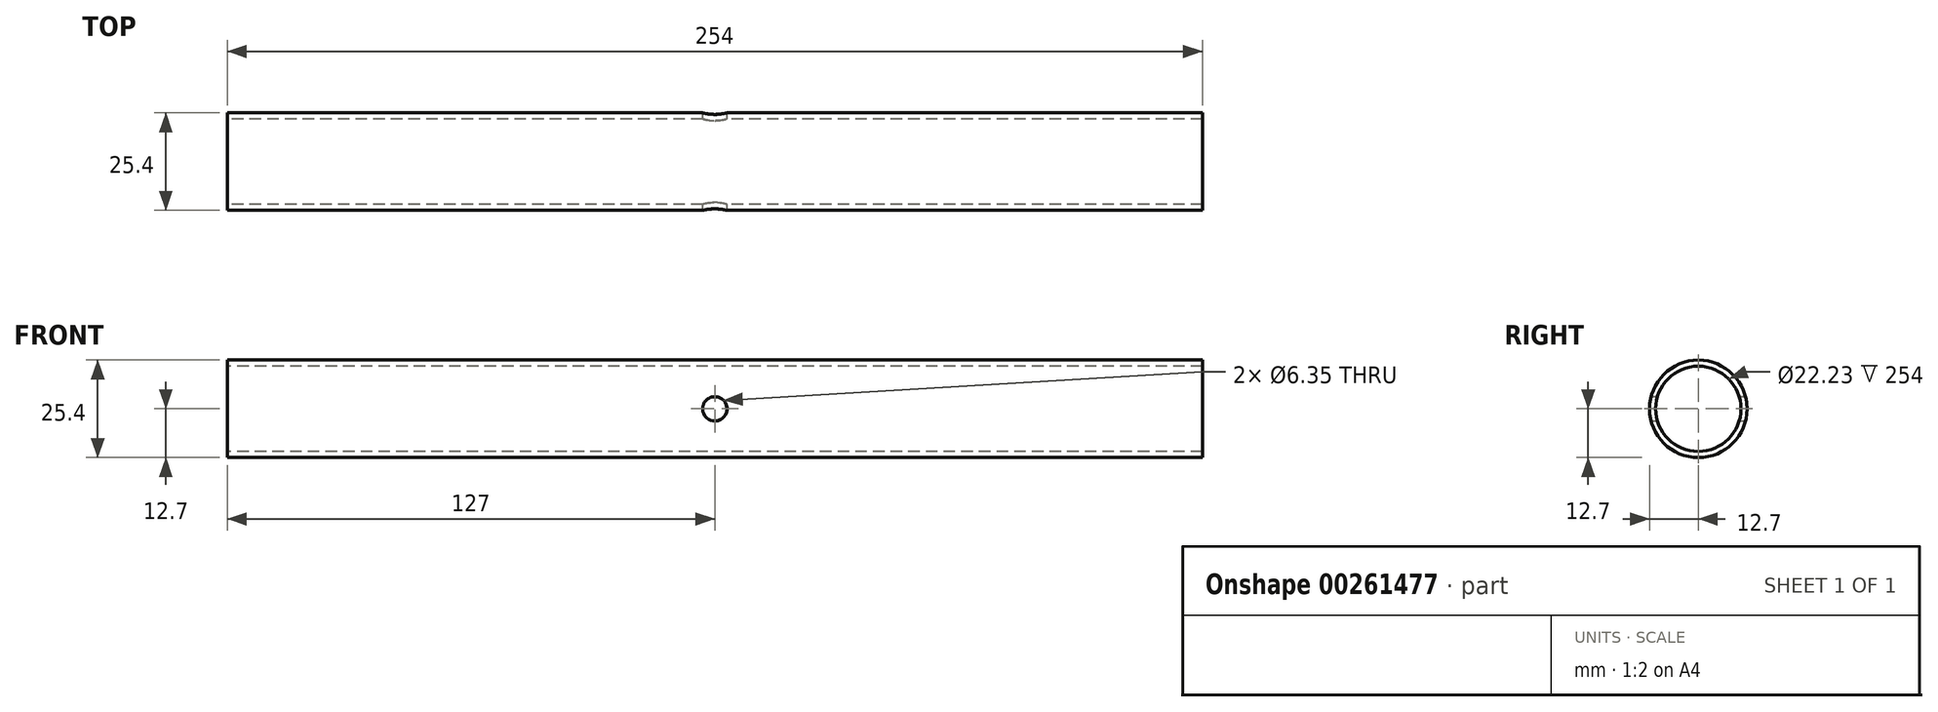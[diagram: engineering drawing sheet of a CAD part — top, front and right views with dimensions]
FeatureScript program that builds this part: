
annotation { "Feature Type Name" : "Feature", "Feature Type Description" : "" }
export const myFeature = defineFeature(function(context is Context, id is Id, definition is map)
    precondition{}
    {
        {
            var Q0;
            Q0=qCreatedBy(makeId("Right.planeOp"),FACE);
            var sketch = newSketch(context, id + "F0", { "sketchPlane" : qUnion([Q0])});
            skCircle(sketch, "E0", {"center": v(-12.7, 0) * mm, "radius": 12.7 * mm});
            skCircle(sketch, "E1", {"center": v(-12.7, 0) * mm, "radius": 11.11 * mm});
            skSolve(sketch);
        }
        {
            var Q0;
            Q0=makeQuery(id+"F0.imprint","IMPRINT",FACE,{"disambiguationData":[TD([[makeQuery(id+"F0.imprint","IMPRINT",EDGE,{"derivedFrom":sQuery(id+"F0.wireOp",EDGE,"E0")}),1.0]])]});
            extrude(context, id + "F3", {"entities" : qUnion([Q0]), "depth" : 177.8 * mm, "hasSecondDirection" : true, "secondDirectionOppositeDirection" : true, "secondDirectionDepth" : 76.2 * mm});
        }
        {
            var Q0;
            Q0=qCreatedBy(makeId("Front.planeOp"),FACE);
            var sketch = newSketch(context, id + "F1", { "sketchPlane" : qUnion([Q0])});
            skCircle(sketch, "E2", {"center": v(50.8, 0) * mm, "radius": 3.18 * mm});
            skSolve(sketch);
        }
        {
            var Q0;
            Q0=makeQuery(id+"F1.imprint","IMPRINT",FACE,{"disambiguationData":[TD([[makeQuery(id+"F1.imprint","IMPRINT",EDGE,{"derivedFrom":sQuery(id+"F1.wireOp",EDGE,"E2")}),1.0]])]});
            extrude(context, id + "F2", {"entities" : qUnion([Q0]), "operationType" : NewBodyOperationType.REMOVE, "depth" : 25.4 * mm});
        }
    });
